# Revit family: J 80
name_source: partatom
category: Equipement spécialisé
revit_build: Autodesk Revit LT 2017 (Build: 20160225_1515(x64)
units: mm (PartAtom-declared; Revit-internal decimal feet)

## family parameters
Basée sur le plan de construction = Non
Cote de connecteur circulaire = Utiliser le rayon
Couper avec des vides une fois chargée = Non
Numéro OmniClass = 23.40.40.14.14.11
Partagée = Non
Point de calcul de pièce = Non
Titre OmniClass = Food Mixers
Toujours verticalement = Oui
Type d'élément = Normal

## types (5) — shared parameters
Apparent Power = 0 VA
Description = CENTRIFUGEUSE
Electrique connexion  Height = 10 mm  [stored 0.0328084 ft]
Electrique connexion Depth = 270 mm  [stored 0.885827 ft]
Electrique connexion Width = 15 mm
Fabricant = ROBOT COUPE
Phase = 1
UP Depth = 725 mm
UP Height = 640 mm  [stored 2.09974 ft]
UP Width = 450 mm  [stored 1.47638 ft]
URL = www.robot-coupe.com
water = Connector
zero-valued in all types: Cold water supply, Cold water supply height, Elec Conn RI Height, Used water, Waste water height

## per-type parameters (varying)
| type | Amps | Cycle | Depth | HP | Height | Modèle | Speeds (Rpm) | Volts | Watts | Weight | Width |
| J 80    230/50/1 | 7 | 50 Hz | 725 mm |  | 505 mm  [stored 1.65682 ft] | J 80 | 3000 | 230 V | 700 W | 12.5 kg | 450 mm  [stored 1.47638 ft] |
| J 80    120/60/1 | 9 | 60 Hz | 535 mm |  | 505 mm  [stored 1.65682 ft] | J 80 | 3000 | 120 V | 700 W | 12.5 kg | 235 mm |
| J 80    220/60/1 | 6 | 60 Hz | 725 mm |  | 505 mm  [stored 1.65682 ft] | J 80 | 3000 | 220 V | 500 W | 12.5 kg | 235 mm |
| J 80    240/50/1 | 7 | 50 Hz | 725 mm |  | 505 mm  [stored 1.65682 ft] | J 80 | 3000 | 240 V | 500 W | 12.5 kg | 450 mm  [stored 1.47638 ft] |
| J 80  USA   120/60/1 |  | 60 Hz | 538 mm | 1 | 506 mm | J 80 USA | 3450 | 120 V | 0 W | 28 lbs | 235 mm |

note: [stored X ft] marks values corroborated as IEEE doubles in the binary element streams (Revit-internal decimal feet)

## geometry (parser evidence)
native form markers: Blend x104, Sweep x5
no freeform markers — native parametric forms only
